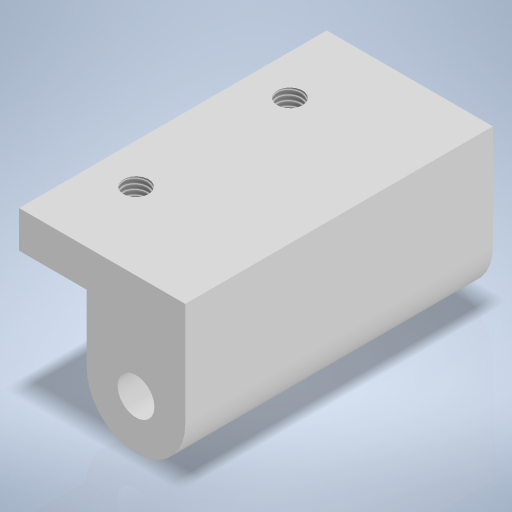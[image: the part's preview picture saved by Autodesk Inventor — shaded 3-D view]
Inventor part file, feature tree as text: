
AUTODESK INVENTOR PART (.ipt)
format: ipt  version: 2024 (Build 280153000, 153)  size: 290,304 bytes
history: native  units: mm
features: sketch x5, hole x3, extrude x2
ambient origin geometry x8: Origin, YZ Plane, XZ Plane, XY Plane, X Axis, Y Axis, Z Axis, Center Point
bodies: Volumenkörper1 (feature_tree)
feature tree (10):
  extrude  "Extrusion1"  Depth=16.0mm
  hole  "Bohrung1"  [1 undecoded]
  extrude  "Extrusion2"  Depth=11.0mm
  hole  "Bohrung2"  [1 undecoded]
  hole  "Bohrung3"  [1 undecoded]
  sketch  "Skizze1"  dims[d0=16.0mm d1=16.0mm]
  sketch  "Skizze2"  dims[d2=6.0mm d3=19.0mm]
  sketch  "Skizze3"  dims[d4=11.0mm d5=17.0mm]
  sketch  "Skizze4"  dims[d6=50.0mm d7=0.0mm]
  sketch  "Skizze5"  dims[d8=6.0mm d9=6.0mm d10=4.0mm d11=2.0mm d12=90.0deg d13=8.0mm d14=20.594885mm d15=6.0mm d16=50.0mm d17=0.0mm d18=9.0mm d19=6.0mm d20=4.0mm d21=2.0mm d22=90.0deg d23=8.0mm d24=0.0mm d25=4.134mm d26=10.0mm d27=4.0mm d28=2.0mm d29=90.0deg d30=8.0mm d31=0.0mm d32=6.5mm d33=12.5mm d34=25.0mm]
note: 3 required parameter values undecoded (feature->parameter linkage not recoverable at this tier; creation-order binding heuristic only, values carry confidence <= 0.55)
